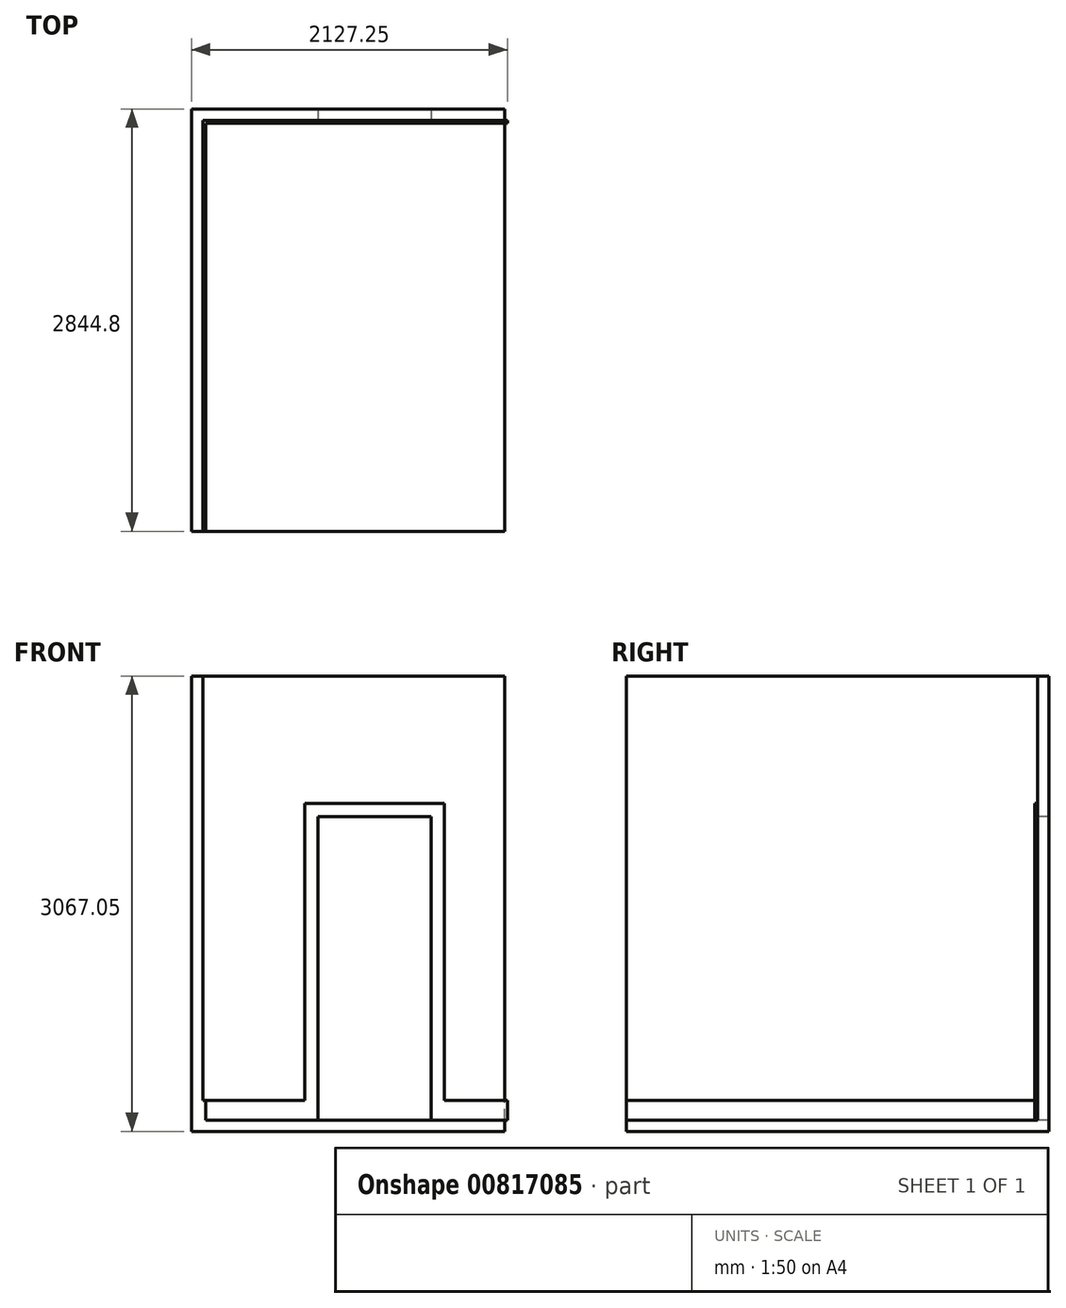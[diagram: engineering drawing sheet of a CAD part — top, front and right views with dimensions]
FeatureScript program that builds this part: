
annotation { "Feature Type Name" : "Feature", "Feature Type Description" : "" }
export const myFeature = defineFeature(function(context is Context, id is Id, definition is map)
    precondition{}
    {
        {
            var Q0;
            Q0=qCreatedBy(makeId("Right.planeOp"),FACE);
            var sketch = newSketch(context, id + "F0", { "sketchPlane" : qUnion([Q0])});
            skLineSegment(sketch, "E0.bottom", {"start": v(0, 0) * mm, "end": v(-2768.6, 0) * mm});
            skLineSegment(sketch, "E0.top", {"start": v(0, 2990.85) * mm, "end": v(-2768.6, 2990.85) * mm});
            skLineSegment(sketch, "E0.left", {"start": v(0, 0) * mm, "end": v(0, 2990.85) * mm});
            skLineSegment(sketch, "E0.right", {"start": v(-2768.6, 0) * mm, "end": v(-2768.6, 2990.85) * mm});
            skSolve(sketch);
        }
        {
            var Q0;
            Q0=makeQuery(id+"F0.imprint","IMPRINT",FACE,{"disambiguationData":[TD([[makeQuery(id+"F0.imprint","IMPRINT",EDGE,{"derivedFrom":sQuery(id+"F0.wireOp",EDGE,"E0.bottom")}),-1.0]])]});
            extrude(context, id + "F1", {"entities" : qUnion([Q0]), "oppositeDirection" : true, "depth" : 76.2 * mm, "offsetDistance" : 25.4 * mm});
        }
        {
            var Q0;
            Q0=makeQuery(id+"F1.opExtrude","SWEPT_FACE",FACE,{"disambiguationData":[OSD([sQuery(id+"F0.wireOp",EDGE,"E0.left")])]});
            var sketch = newSketch(context, id + "F2", { "sketchPlane" : qUnion([Q0])});
            skLineSegment(sketch, "E1.bottom", {"start": v(76.2, 0) * mm, "end": v(-2032, 0) * mm});
            skLineSegment(sketch, "E1.top", {"start": v(76.2, 2990.85) * mm, "end": v(-2032, 2990.85) * mm});
            skLineSegment(sketch, "E1.left", {"start": v(76.2, 0) * mm, "end": v(76.2, 2990.85) * mm});
            skLineSegment(sketch, "E1.right", {"start": v(-2032, 0) * mm, "end": v(-2032, 2990.85) * mm});
            skSolve(sketch);
        }
        {
            var Q0;
            Q0 = qSketchRegion(id + "F2", true);
            extrude(context, id + "F3", {"entities" : qUnion([Q0]), "operationType" : NewBodyOperationType.ADD, "depth" : 76.2 * mm, "offsetDistance" : 25.4 * mm});
        }
        {
            var Q0;
            Q0=makeQuery(id+"F3.boolean.opBoolean","MERGE",FACE,{"derivedFrom":[makeQuery(id+"F1.opExtrude","SWEPT_FACE",FACE,{"disambiguationData":[OSD([sQuery(id+"F0.wireOp",EDGE,"E0.bottom")])]}),makeQuery(id+"F3.opExtrude","SWEPT_FACE",FACE,{"disambiguationData":[OSD([sQuery(id+"F2.wireOp",EDGE,"E1.bottom")])]})]});
            var sketch = newSketch(context, id + "F4", { "sketchPlane" : qUnion([Q0])});
            skLineSegment(sketch, "E2.bottom", {"start": v(-76.2, -76.2) * mm, "end": v(2032, -76.2) * mm});
            skLineSegment(sketch, "E2.top", {"start": v(-76.2, 2768.6) * mm, "end": v(2032, 2768.6) * mm});
            skLineSegment(sketch, "E2.left", {"start": v(-76.2, -76.2) * mm, "end": v(-76.2, 2768.6) * mm});
            skLineSegment(sketch, "E2.right", {"start": v(2032, -76.2) * mm, "end": v(2032, 2768.6) * mm});
            skSolve(sketch);
        }
        {
            var Q0;
            Q0 = qSketchRegion(id + "F4", true);
            extrude(context, id + "F5", {"entities" : qUnion([Q0]), "operationType" : NewBodyOperationType.ADD, "depth" : 76.2 * mm, "offsetDistance" : 25.4 * mm});
        }
        {
            var Q0;
            Q0=makeQuery(id+"F3.opExtrude","CAP_FACE",FACE,{"disambiguationData":[OSD([sQuery(id+"F2.wireOp",EDGE,"E1.bottom"),sQuery(id+"F2.wireOp",EDGE,"E1.top"),sQuery(id+"F2.wireOp",EDGE,"E1.left"),sQuery(id+"F2.wireOp",EDGE,"E1.right")])],"isStart":true});
            var sketch = newSketch(context, id + "F6", { "sketchPlane" : qUnion([Q0])});
            skPoint(sketch, "E3", {"position": v(774.7, 0) * mm});
            skLineSegment(sketch, "E4.bottom", {"start": v(774.7, 0) * mm, "end": v(1536.7, 0) * mm});
            skLineSegment(sketch, "E4.top", {"start": v(774.7, 2044.7) * mm, "end": v(1536.7, 2044.7) * mm});
            skLineSegment(sketch, "E4.left", {"start": v(774.7, 0) * mm, "end": v(774.7, 2044.7) * mm});
            skLineSegment(sketch, "E4.right", {"start": v(1536.7, 0) * mm, "end": v(1536.7, 2044.7) * mm});
            skSolve(sketch);
        }
        {
            var Q0;
            Q0=makeQuery(id+"F6.imprint","IMPRINT",FACE,{"disambiguationData":[TD([[makeQuery(id+"F6.imprint","IMPRINT",EDGE,{"derivedFrom":sQuery(id+"F6.wireOp",EDGE,"E4.bottom")}),1.0]])]});
            extrude(context, id + "F7", {"entities" : qUnion([Q0]), "operationType" : NewBodyOperationType.REMOVE, "oppositeDirection" : true, "depth" : 76.2 * mm, "offsetDistance" : 25.4 * mm});
        }
        {
            var Q0;
            Q0=makeQuery(id+"F5.boolean.opBoolean","MERGE",FACE,{"derivedFrom":[makeQuery(id+"F1.opExtrude","SWEPT_FACE",FACE,{"disambiguationData":[OSD([sQuery(id+"F0.wireOp",EDGE,"E0.right")])]}),makeQuery(id+"F5.opExtrude","SWEPT_FACE",FACE,{"disambiguationData":[OSD([sQuery(id+"F4.wireOp",EDGE,"E2.top")])]})]});
            var sketch = newSketch(context, id + "F8", { "sketchPlane" : qUnion([Q0])});
            skLineSegment(sketch, "E5.bottom", {"start": v(0, 0) * mm, "end": v(19.05, 0) * mm});
            skLineSegment(sketch, "E5.top", {"start": v(0, 133.35) * mm, "end": v(19.05, 133.35) * mm});
            skLineSegment(sketch, "E5.left", {"start": v(0, 0) * mm, "end": v(0, 133.35) * mm});
            skLineSegment(sketch, "E5.right", {"start": v(19.05, 0) * mm, "end": v(19.05, 133.35) * mm});
            skSolve(sketch);
        }
        {
            var Q0;
            Q0=makeQuery(id+"F8.imprint","IMPRINT",FACE,{"disambiguationData":[TD([[makeQuery(id+"F8.imprint","IMPRINT",EDGE,{"derivedFrom":sQuery(id+"F8.wireOp",EDGE,"E5.bottom")}),1.0]])]});
            extrude(context, id + "F9", {"entities" : qUnion([Q0]), "operationType" : NewBodyOperationType.ADD, "oppositeDirection" : true, "depth" : 2768.6 * mm, "offsetDistance" : 25.4 * mm});
        }
        {
            var Q0;
            Q0=makeQuery(id+"F9.opExtrude","SWEPT_FACE",FACE,{"disambiguationData":[OSD([sQuery(id+"F8.wireOp",EDGE,"E5.right")])]});
            var sketch = newSketch(context, id + "F10", { "sketchPlane" : qUnion([Q0])});
            skLineSegment(sketch, "E6.bottom", {"start": v(0, 0) * mm, "end": v(-19.05, 0) * mm});
            skLineSegment(sketch, "E6.top", {"start": v(0, 133.35) * mm, "end": v(-19.05, 133.35) * mm});
            skLineSegment(sketch, "E6.left", {"start": v(0, 0) * mm, "end": v(0, 133.35) * mm});
            skLineSegment(sketch, "E6.right", {"start": v(-19.05, 0) * mm, "end": v(-19.05, 133.35) * mm});
            skSolve(sketch);
        }
        {
            var Q0;
            Q0=makeQuery(id+"F10.imprint","IMPRINT",FACE,{"disambiguationData":[TD([[makeQuery(id+"F10.imprint","IMPRINT",EDGE,{"derivedFrom":sQuery(id+"F10.wireOp",EDGE,"E6.bottom")}),-1.0]])]});
            extrude(context, id + "F11", {"entities" : qUnion([Q0]), "operationType" : NewBodyOperationType.ADD, "depth" : 2032 * mm, "offsetDistance" : 25.4 * mm});
        }
        {
            var Q0;
            Q0=makeQuery(id+"F11.boolean.opBoolean","MERGE",FACE,{"derivedFrom":[makeQuery(id+"F9.opExtrude","SWEPT_FACE",FACE,{"disambiguationData":[OSD([sQuery(id+"F8.wireOp",EDGE,"E5.top")])]}),makeQuery(id+"F11.opExtrude","SWEPT_FACE",FACE,{"disambiguationData":[OSD([sQuery(id+"F10.wireOp",EDGE,"E6.top")])]})]});
            var sketch = newSketch(context, id + "F12", { "sketchPlane" : qUnion([Q0])});
            skPoint(sketch, "E7", {"position": v(685.8, 0) * mm});
            skLineSegment(sketch, "E8.bottom", {"start": v(685.8, 0) * mm, "end": v(1625.6, 0) * mm});
            skLineSegment(sketch, "E8.top", {"start": v(685.8, -19.05) * mm, "end": v(1625.6, -19.05) * mm});
            skLineSegment(sketch, "E8.left", {"start": v(685.8, 0) * mm, "end": v(685.8, -19.05) * mm});
            skLineSegment(sketch, "E8.right", {"start": v(1625.6, 0) * mm, "end": v(1625.6, -19.05) * mm});
            skSolve(sketch);
        }
        {
            var Q0;
            Q0 = qSketchRegion(id + "F12", true);
            extrude(context, id + "F13", {"entities" : qUnion([Q0]), "operationType" : NewBodyOperationType.ADD, "depth" : 2000.25 * mm, "offsetDistance" : 25.4 * mm});
        }
        {
            var Q0;
            Q0 = qSketchRegion(id + "F6", true);
            extrude(context, id + "F14", {"entities" : qUnion([Q0]), "operationType" : NewBodyOperationType.REMOVE, "depth" : 19.05 * mm, "offsetDistance" : 25.4 * mm});
        }
    });
